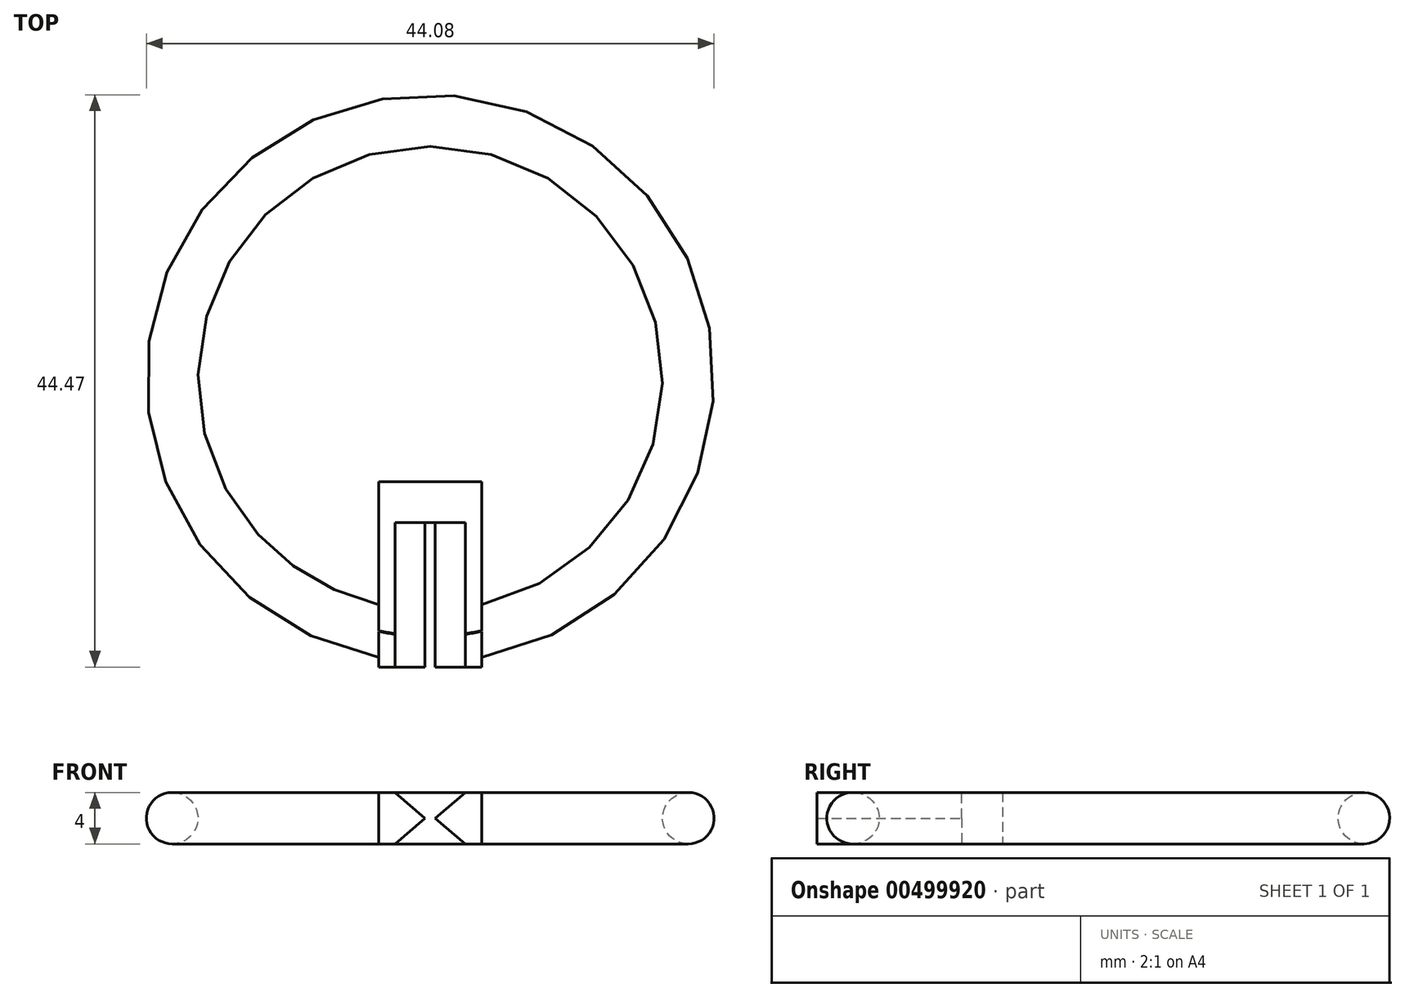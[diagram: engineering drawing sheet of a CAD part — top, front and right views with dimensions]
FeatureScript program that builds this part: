
annotation { "Feature Type Name" : "Feature", "Feature Type Description" : "" }
export const myFeature = defineFeature(function(context is Context, id is Id, definition is map)
    precondition{}
    {
        {
            var Q0;
            Q0=qCreatedBy(makeId("Top.planeOp"),FACE);
            var sketch = newSketch(context, id + "F0", { "sketchPlane" : qUnion([Q0])});
            skCircle(sketch, "E0", {"center": v(0, 0) * mm, "radius": 18 * mm});
            skSolve(sketch);
        }
        {
            var Q0;
            Q0=qCreatedBy(makeId("Front.planeOp"),FACE);
            var sketch = newSketch(context, id + "F1", { "sketchPlane" : qUnion([Q0])});
            skCircle(sketch, "E1", {"center": v(-20.04, 0) * mm, "radius": 2 * mm});
            skPoint(sketch, "E2.start.orphan", {"position": v(-18.04, 0) * mm});
            skSolve(sketch);
        }
        {
            var Q0;
            Q0=makeQuery(id+"F1.imprint","IMPRINT",FACE,{"disambiguationData":[TD([[makeQuery(id+"F1.imprint","IMPRINT",EDGE,{"derivedFrom":sQuery(id+"F1.wireOp",EDGE,"E1")}),1.0]])]});
            var Q1;
            Q1=sQuery(id+"F0.wireOp",EDGE,"E0");
            sweep(context, id + "F2", {"profiles" : qUnion([Q0]), "path" : qUnion([Q1])});
        }
        {
            var Q0;
            Q0=qCreatedBy(makeId("Top.planeOp"),FACE);
            var sketch = newSketch(context, id + "F3", { "sketchPlane" : qUnion([Q0])});
            skLineSegment(sketch, "E3", {"start": v(0, -8.03) * mm, "end": v(4, -8.03) * mm});
            skLineSegment(sketch, "E4", {"start": v(4, -8.03) * mm, "end": v(4, -19.93) * mm});
            skLineSegment(sketch, "E5.MirrorCS", {"start": v(0, -8.03) * mm, "end": v(-4, -8.03) * mm});
            skLineSegment(sketch, "E6.MirrorCS", {"start": v(-4, -8.03) * mm, "end": v(-4, -19.93) * mm});
            skPoint(sketch, "E7.orphan", {"position": v(4, -21.62) * mm});
            skPoint(sketch, "E8.orphan", {"position": v(0, -22.03) * mm});
            skPoint(sketch, "E9.orphan", {"position": v(-4, -21.62) * mm});
            skLineSegment(sketch, "E10", {"start": v(4, -19.93) * mm, "end": v(4, -22.43) * mm});
            skLineSegment(sketch, "E11", {"start": v(4, -22.43) * mm, "end": v(-4, -22.43) * mm});
            skLineSegment(sketch, "E12", {"start": v(-4, -22.43) * mm, "end": v(-4, -19.93) * mm});
            skSolve(sketch);
        }
        {
            var Q0;
            Q0=qSketchRegion(id+"F3",true);
            extrude(context, id + "F4", {"entities" : qUnion([Q0]), "operationType" : NewBodyOperationType.ADD, "depth" : 2 * mm, "hasSecondDirection" : true, "secondDirectionOppositeDirection" : true, "secondDirectionDepth" : 2 * mm});
        }
        {
            var Q0;
            Q0=qCreatedBy(makeId("Front.planeOp"),FACE);
            var sketch = newSketch(context, id + "F5", { "sketchPlane" : qUnion([Q0])});
            skLineSegment(sketch, "E13", {"start": v(2.75, -2.01) * mm, "end": v(-2.75, -2.01) * mm});
            skLineSegment(sketch, "E14", {"start": v(0, 0) * mm, "end": v(0.4, 0) * mm});
            skLineSegment(sketch, "E15.MirrorCS", {"start": v(0, 0) * mm, "end": v(-0.4, 0) * mm});
            skLineSegment(sketch, "E16.MirrorCS", {"start": v(2.75, 2.01) * mm, "end": v(-2.75, 2.01) * mm});
            skPoint(sketch, "E17.end.orphan", {"position": v(-3.98, 1.99) * mm});
            skLineSegment(sketch, "E18", {"start": v(0.4, 0) * mm, "end": v(2.75, -2.01) * mm});
            skLineSegment(sketch, "E19.MirrorCS", {"start": v(0.4, 0) * mm, "end": v(2.75, 2.01) * mm});
            skLineSegment(sketch, "E20.MirrorCS", {"start": v(-0.4, 0) * mm, "end": v(-2.75, 2.01) * mm});
            skLineSegment(sketch, "E21.MirrorCS", {"start": v(-0.4, 0) * mm, "end": v(-2.75, -2.01) * mm});
            skPoint(sketch, "E22.MirrorCS.start.orphan", {"position": v(3.98, -2.01) * mm});
            skPoint(sketch, "E23.orphan", {"position": v(-3.98, -2.01) * mm});
            skPoint(sketch, "E24.end.orphan", {"position": v(3.98, 1.99) * mm});
            skPoint(sketch, "E24.start.orphan", {"position": v(3.98, 2.01) * mm});
            skPoint(sketch, "E25.start.orphan", {"position": v(-3.98, 2.01) * mm});
            skSolve(sketch);
        }
        {
            var Q0;
            Q0=makeQuery(id+"F5.imprint","IMPRINT",FACE,{"disambiguationData":[TD([[makeQuery(id+"F5.imprint","IMPRINT",EDGE,{"derivedFrom":sQuery(id+"F5.wireOp",EDGE,"E13")}),-1.0]])]});
            var Q1;
            Q1=makeQuery(id+"F5.imprint","IMPRINT",FACE,{"disambiguationData":[TD([[makeQuery(id+"F5.imprint","IMPRINT",EDGE,{"derivedFrom":sQuery(id+"F5.wireOp",EDGE,"E14")}),1.0]])]});
            extrude(context, id + "F6", {"entities" : qUnion([Q0, Q1]), "operationType" : NewBodyOperationType.REMOVE, "depth" : 36.8 * mm, "hasSecondDirection" : true, "secondDirectionOppositeDirection" : false, "secondDirectionDepth" : 11.2 * mm});
        }
    });
